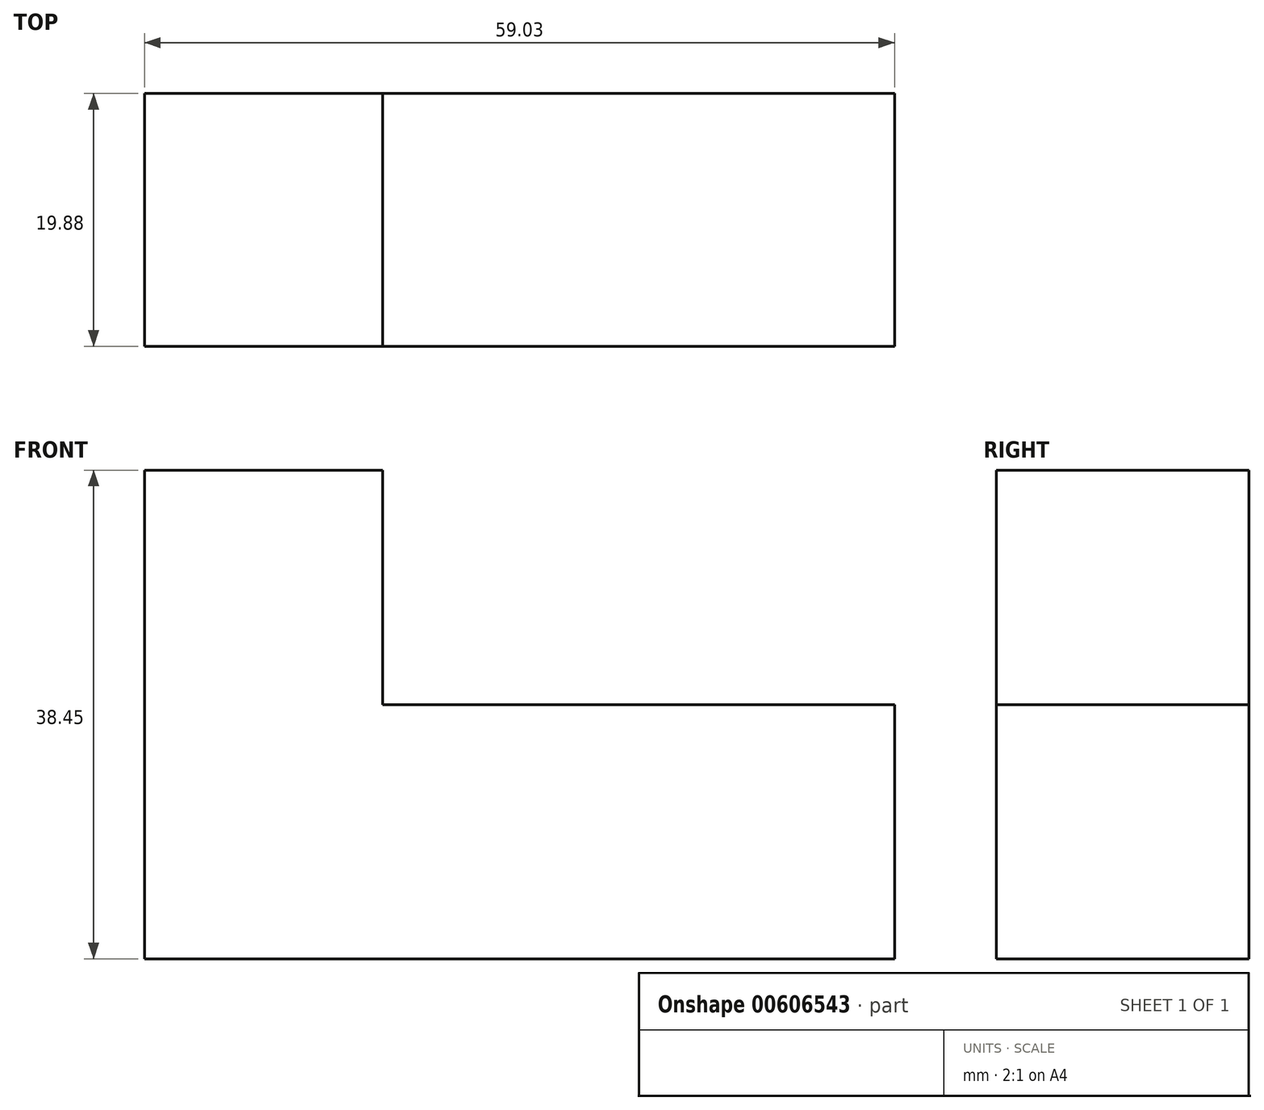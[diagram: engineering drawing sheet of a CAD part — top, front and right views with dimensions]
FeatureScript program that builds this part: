
annotation { "Feature Type Name" : "Feature", "Feature Type Description" : "" }
export const myFeature = defineFeature(function(context is Context, id is Id, definition is map)
    precondition{}
    {
        {
            var Q0;
            Q0=qCreatedBy(makeId("Front.planeOp"),FACE);
            var sketch = newSketch(context, id + "F0", { "sketchPlane" : qUnion([Q0])});
            skLineSegment(sketch, "E0", {"start": v(0, 0) * mm, "end": v(59.03, 0) * mm});
            skLineSegment(sketch, "E1", {"start": v(59.03, 0) * mm, "end": v(59.03, 20) * mm});
            skLineSegment(sketch, "E2", {"start": v(59.03, 20) * mm, "end": v(18.74, 20) * mm});
            skLineSegment(sketch, "E3", {"start": v(18.74, 20) * mm, "end": v(18.74, 38.45) * mm});
            skLineSegment(sketch, "E4", {"start": v(18.74, 38.45) * mm, "end": v(0, 38.45) * mm});
            skLineSegment(sketch, "E5", {"start": v(0, 38.45) * mm, "end": v(0, 0) * mm});
            skSolve(sketch);
        }
        {
            var Q0;
            Q0=makeQuery(id+"F0.imprint","IMPRINT",FACE,{"disambiguationData":[TD([[makeQuery(id+"F0.imprint","IMPRINT",EDGE,{"derivedFrom":sQuery(id+"F0.wireOp",EDGE,"E0")}),1.0]])]});
            extrude(context, id + "F1", {"entities" : qUnion([Q0]), "depth" : 19.88 * mm, "offsetDistance" : 25.4 * mm});
        }
    });
